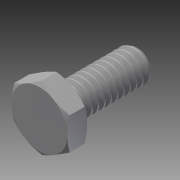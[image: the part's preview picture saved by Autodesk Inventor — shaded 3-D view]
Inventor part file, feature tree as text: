
AUTODESK INVENTOR PART (.ipt)
format: ipt  version: 2014 SP1 (Build 180222100, 222)  size: 438,784 bytes
history: native  units: in
note: dims shown in document units (in); Inventor stores cm internally (conversion verified against a paired STEP export)
features: extrude x1, other x1, imported_body x1
ambient origin geometry x8: Origin, YZ Plane, XZ Plane, XY Plane, X Axis, Y Axis, Z Axis, Center Point
bodies: Body1 (feature_tree)
feature tree (3):
  extrude  "Extrude14"  [1 undecoded]
  other  "92620A5391"
  imported_body  "Base1"
note: 1 required parameter value undecoded (feature->parameter linkage not recoverable at this tier; creation-order binding heuristic only, values carry confidence <= 0.55)
